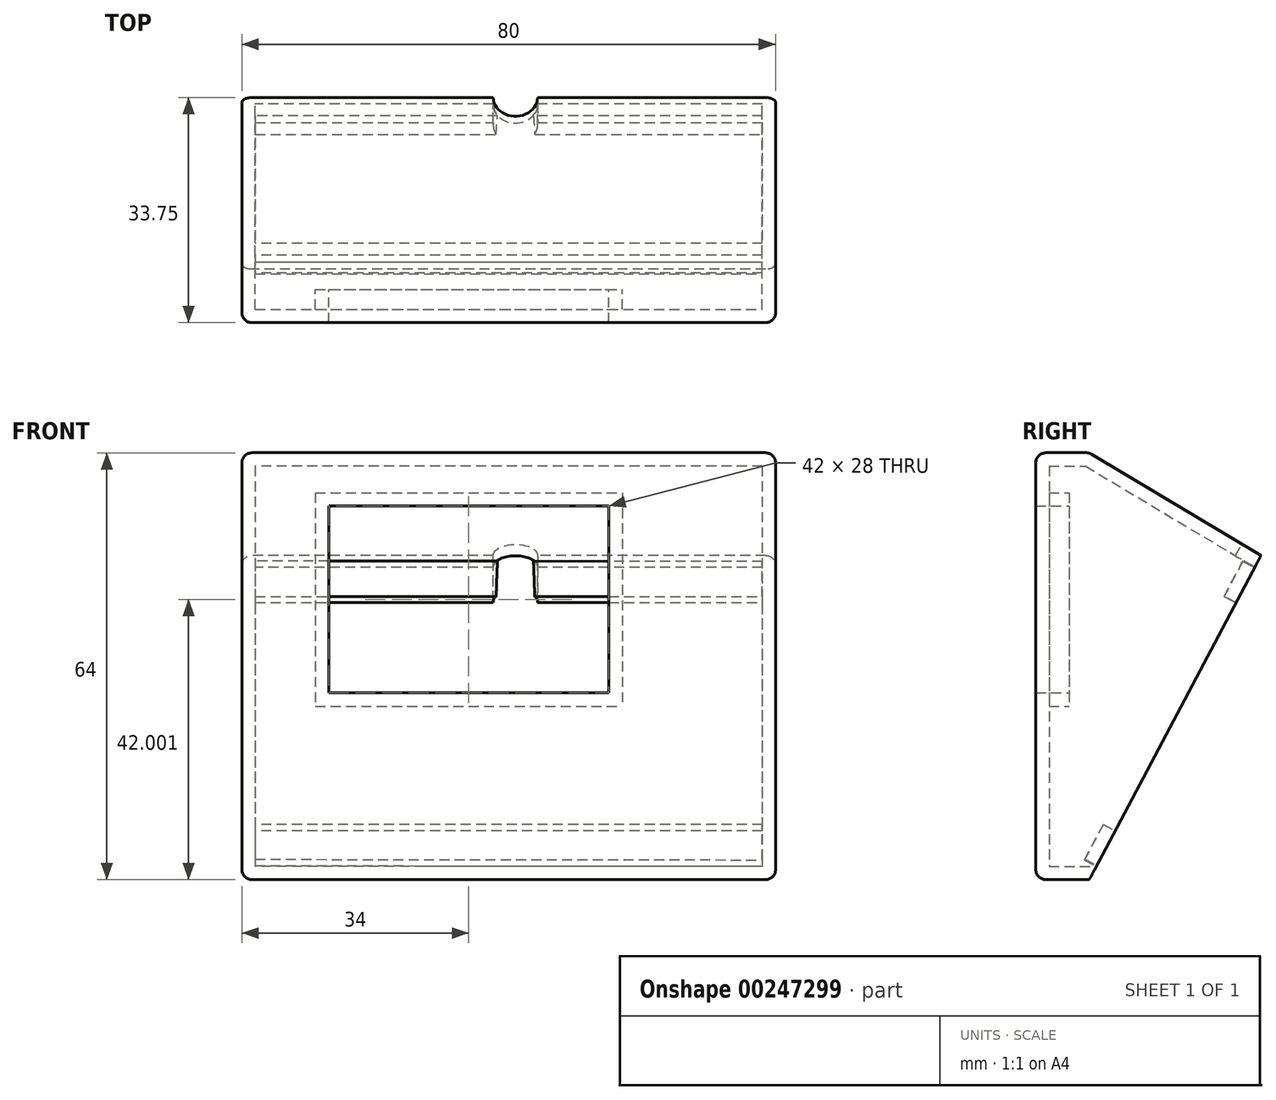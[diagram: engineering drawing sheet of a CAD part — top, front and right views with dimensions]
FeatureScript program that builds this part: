
annotation { "Feature Type Name" : "Feature", "Feature Type Description" : "" }
export const myFeature = defineFeature(function(context is Context, id is Id, definition is map)
    precondition{}
    {
        {
            var Q0;
            Q0=qCreatedBy(makeId("Front.planeOp"),FACE);
            var sketch = newSketch(context, id + "F0", { "sketchPlane" : qUnion([Q0])});
            skLineSegment(sketch, "E0.bottom", {"start": v(-41, 33.96) * mm, "end": v(39, 33.96) * mm});
            skLineSegment(sketch, "E0.top", {"start": v(-41, -30.04) * mm, "end": v(39, -30.04) * mm});
            skLineSegment(sketch, "E0.left", {"start": v(-41, 33.96) * mm, "end": v(-41, -30.04) * mm});
            skLineSegment(sketch, "E0.right", {"start": v(39, 33.96) * mm, "end": v(39, -30.04) * mm});
            skLineSegment(sketch, "E1.bottom", {"start": v(-28, 25.96) * mm, "end": v(14, 25.96) * mm});
            skLineSegment(sketch, "E1.top", {"start": v(-28, -2.04) * mm, "end": v(14, -2.04) * mm});
            skLineSegment(sketch, "E1.left", {"start": v(-28, 25.96) * mm, "end": v(-28, -2.04) * mm});
            skLineSegment(sketch, "E1.right", {"start": v(14, 25.96) * mm, "end": v(14, -2.04) * mm});
            skSolve(sketch);
        }
        {
            var Q0;
            Q0=makeQuery(id+"F0.imprint","IMPRINT",FACE,{"disambiguationData":[TD([[makeQuery(id+"F0.imprint","IMPRINT",EDGE,{"derivedFrom":sQuery(id+"F0.wireOp",EDGE,"E0.bottom")}),-1.0]])]});
            extrude(context, id + "F1", {"entities" : qUnion([Q0]), "depth" : 3 * mm});
        }
        {
            var Q0;
            Q0=makeQuery(id+"F1.opExtrude","SWEPT_FACE",FACE,{"disambiguationData":[OSD([sQuery(id+"F0.wireOp",EDGE,"E0.left")])]});
            cPlane(context, id + "F2", {"entities" : qUnion([Q0]), "cplaneType" : CPlaneType.OFFSET, "offset" : 0 * mm, "width" : 150 * mm, "height" : 150 * mm});
        }
        {
            var Q0;
            Q0=qCreatedBy(id+"F2.planeOp",FACE);
            var sketch = newSketch(context, id + "F3", { "sketchPlane" : qUnion([Q0])});
            skLineSegment(sketch, "E2", {"start": v(0, 33.96) * mm, "end": v(-5, 33.96) * mm});
            skLineSegment(sketch, "E3", {"start": v(-5, 33.96) * mm, "end": v(-30.75, 18.56) * mm});
            skLineSegment(sketch, "E4", {"start": v(-30.75, 18.56) * mm, "end": v(-5, -30.04) * mm});
            skLineSegment(sketch, "E5", {"start": v(-5, -30.04) * mm, "end": v(0, -30.04) * mm});
            skLineSegment(sketch, "E6", {"start": v(0, -30.04) * mm, "end": v(0, 33.96) * mm});
            skSolve(sketch);
        }
        {
            var Q0;
            Q0=makeQuery(id+"F3.imprint","IMPRINT",FACE,{"disambiguationData":[TD([[makeQuery(id+"F3.imprint","IMPRINT",EDGE,{"derivedFrom":sQuery(id+"F3.wireOp",EDGE,"E2")}),1.0]])]});
            extrude(context, id + "F4", {"entities" : qUnion([Q0]), "operationType" : NewBodyOperationType.ADD, "oppositeDirection" : true, "depth" : 80 * mm});
        }
        {
            var Q0;
            Q0=makeQuery(id+"F4.opExtrude","SWEPT_FACE",FACE,{"disambiguationData":[OSD([sQuery(id+"F3.wireOp",EDGE,"E4")])]});
            shell(context, id + "F5", {"entities" : qUnion([Q0]), "thickness" : 2 * mm});
        }
        {
            var Q0;
            Q0=makeQuery(id+"F0.imprint","IMPRINT",FACE,{"disambiguationData":[TD([[makeQuery(id+"F0.imprint","IMPRINT",EDGE,{"derivedFrom":sQuery(id+"F0.wireOp",EDGE,"tYb5kqSu-YFri-1jrc-o4Oq-ESpyQk4ThZfy")}),1.0]])]});
            var Q1;
            Q1=makeQuery(id+"F0.imprint","IMPRINT",FACE,{"disambiguationData":[TD([[makeQuery(id+"F0.imprint","IMPRINT",EDGE,{"derivedFrom":sQuery(id+"F0.wireOp",EDGE,"0d1e089b-857e-4050-88c1-200f67481d80")}),1.0]])]});
            var Q2;
            Q2=makeQuery(id+"F0.imprint","IMPRINT",FACE,{"disambiguationData":[TD([[makeQuery(id+"F0.imprint","IMPRINT",EDGE,{"derivedFrom":sQuery(id+"F0.wireOp",EDGE,"e7074c25-9ab7-490e-b367-edef4363bac3")}),1.0]])]});
            var Q3;
            Q3=makeQuery(id+"F0.imprint","IMPRINT",FACE,{"disambiguationData":[TD([[makeQuery(id+"F0.imprint","IMPRINT",EDGE,{"derivedFrom":sQuery(id+"F0.wireOp",EDGE,"ab4bee96-640a-41a6-9e68-64fc1a0f792d")}),1.0]])]});
            var Q4;
            Q4=makeQuery(id+"F0.imprint","IMPRINT",FACE,{"disambiguationData":[TD([[makeQuery(id+"F0.imprint","IMPRINT",EDGE,{"derivedFrom":sQuery(id+"F0.wireOp",EDGE,"636ad2b5-b186-44ca-803b-94d0a85fc76c")}),1.0]])]});
            var Q5;
            Q5=makeQuery(id+"F0.imprint","IMPRINT",FACE,{"disambiguationData":[TD([[makeQuery(id+"F0.imprint","IMPRINT",EDGE,{"derivedFrom":sQuery(id+"F0.wireOp",EDGE,"E1.bottom")}),-1.0]])]});
            extrude(context, id + "F6", {"entities" : qUnion([Q0, Q1, Q2, Q3, Q4, Q5]), "operationType" : NewBodyOperationType.REMOVE, "oppositeDirection" : true, "depth" : 5 * mm});
        }
        {
            var Q0;
            Q0=makeQuery(id+"F1.opExtrude","CAP_EDGE",EDGE,{"disambiguationData":[OSD([sQuery(id+"F0.wireOp",EDGE,"E0.right")])],"isStart":false});
            var Q1;
            Q1=makeQuery(id+"F4.boolean.opBoolean","MERGE",EDGE,{"derivedFrom":[makeQuery(id+"F1.opExtrude","SWEPT_EDGE",EDGE,{"disambiguationData":[OSD([sQuery(id+"F0.wireOp",EDGE,"E0.top"),sQuery(id+"F0.wireOp",EDGE,"E0.right")])]}),makeQuery(id+"F4.opExtrude","CAP_EDGE",EDGE,{"disambiguationData":[OSD([sQuery(id+"F3.wireOp",EDGE,"E5")])],"isStart":false})]});
            var Q2;
            Q2=makeQuery(id+"F1.opExtrude","CAP_EDGE",EDGE,{"disambiguationData":[OSD([sQuery(id+"F0.wireOp",EDGE,"E0.top")])],"isStart":false});
            var Q3;
            Q3=makeQuery(id+"F4.boolean.opBoolean","MERGE",EDGE,{"derivedFrom":[makeQuery(id+"F1.opExtrude","SWEPT_EDGE",EDGE,{"disambiguationData":[OSD([sQuery(id+"F0.wireOp",EDGE,"E0.bottom"),sQuery(id+"F0.wireOp",EDGE,"E0.right")])]}),makeQuery(id+"F4.opExtrude","CAP_EDGE",EDGE,{"disambiguationData":[OSD([sQuery(id+"F3.wireOp",EDGE,"E2")])],"isStart":false})]});
            var Q4;
            Q4=makeQuery(id+"F4.opExtrude","CAP_EDGE",EDGE,{"disambiguationData":[OSD([sQuery(id+"F3.wireOp",EDGE,"E3")])],"isStart":false});
            var Q5;
            Q5=makeQuery(id+"F1.opExtrude","CAP_EDGE",EDGE,{"disambiguationData":[OSD([sQuery(id+"F0.wireOp",EDGE,"E0.bottom")])],"isStart":false});
            var Q6;
            Q6=makeQuery(id+"F4.opExtrude","SWEPT_EDGE",EDGE,{"disambiguationData":[OSD([sQuery(id+"F3.wireOp",EDGE,"E2"),sQuery(id+"F3.wireOp",EDGE,"E3")])]});
            var Q7;
            Q7=makeQuery(id+"F1.opExtrude","CAP_EDGE",EDGE,{"disambiguationData":[OSD([sQuery(id+"F0.wireOp",EDGE,"E0.left")])],"isStart":false});
            var Q8;
            Q8=makeQuery(id+"F4.boolean.opBoolean","MERGE",EDGE,{"derivedFrom":[makeQuery(id+"F1.opExtrude","SWEPT_EDGE",EDGE,{"disambiguationData":[OSD([sQuery(id+"F0.wireOp",EDGE,"E0.bottom"),sQuery(id+"F0.wireOp",EDGE,"E0.left")])]}),makeQuery(id+"F4.opExtrude","CAP_EDGE",EDGE,{"disambiguationData":[OSD([sQuery(id+"F3.wireOp",EDGE,"E2")])],"isStart":true})]});
            var Q9;
            Q9=makeQuery(id+"F4.opExtrude","CAP_EDGE",EDGE,{"disambiguationData":[OSD([sQuery(id+"F3.wireOp",EDGE,"E3")])],"isStart":true});
            var Q10;
            Q10=makeQuery(id+"F4.boolean.opBoolean","MERGE",EDGE,{"derivedFrom":[makeQuery(id+"F1.opExtrude","SWEPT_EDGE",EDGE,{"disambiguationData":[OSD([sQuery(id+"F0.wireOp",EDGE,"E0.top"),sQuery(id+"F0.wireOp",EDGE,"E0.left")])]}),makeQuery(id+"F4.opExtrude","CAP_EDGE",EDGE,{"disambiguationData":[OSD([sQuery(id+"F3.wireOp",EDGE,"E5")])],"isStart":true})]});
            fillet(context, id + "F7", {"entities" : qUnion([Q0, Q1, Q2, Q3, Q4, Q5, Q6, Q7, Q8, Q9, Q10]), "radius" : 1.5 * mm, "tangentPropagation" : true, "allowEdgeOverflow" : false});
        }
        {
            var Q0;
            Q0=makeQuery(id+"F1.opExtrude","SWEPT_BODY",BODY,{"disambiguationData":[OSD([sQuery(id+"F0.wireOp",EDGE,"E0.bottom"),sQuery(id+"F0.wireOp",EDGE,"E0.top"),sQuery(id+"F0.wireOp",EDGE,"E0.left"),sQuery(id+"F0.wireOp",EDGE,"E0.right"),sQuery(id+"F0.wireOp",EDGE,"tYb5kqSu-YFri-1jrc-o4Oq-ESpyQk4ThZfy"),sQuery(id+"F0.wireOp",EDGE,"0d1e089b-857e-4050-88c1-200f67481d80"),sQuery(id+"F0.wireOp",EDGE,"e7074c25-9ab7-490e-b367-edef4363bac3"),sQuery(id+"F0.wireOp",EDGE,"ab4bee96-640a-41a6-9e68-64fc1a0f792d"),sQuery(id+"F0.wireOp",EDGE,"636ad2b5-b186-44ca-803b-94d0a85fc76c"),sQuery(id+"F0.wireOp",EDGE,"E1.bottom"),sQuery(id+"F0.wireOp",EDGE,"E1.top"),sQuery(id+"F0.wireOp",EDGE,"E1.left"),sQuery(id+"F0.wireOp",EDGE,"E1.right")])]});
            transform(context, id + "F8", {"entities" : qUnion([Q0]), "transformType" : TransformType.TRANSLATION_3D, "dx" : 0 * mm, "dy" : 0 * mm, "dz" : 0 * mm, "makeCopy" : true});
        }
        {
            var Q0;
            Q0=makeQuery(id+"F8.opPattern","COPY",BODY,{"derivedFrom":makeQuery(id+"F1.opExtrude","SWEPT_BODY",BODY,{"disambiguationData":[OSD([sQuery(id+"F0.wireOp",EDGE,"E0.bottom"),sQuery(id+"F0.wireOp",EDGE,"E0.top"),sQuery(id+"F0.wireOp",EDGE,"E0.left"),sQuery(id+"F0.wireOp",EDGE,"E0.right"),sQuery(id+"F0.wireOp",EDGE,"tYb5kqSu-YFri-1jrc-o4Oq-ESpyQk4ThZfy"),sQuery(id+"F0.wireOp",EDGE,"0d1e089b-857e-4050-88c1-200f67481d80"),sQuery(id+"F0.wireOp",EDGE,"e7074c25-9ab7-490e-b367-edef4363bac3"),sQuery(id+"F0.wireOp",EDGE,"ab4bee96-640a-41a6-9e68-64fc1a0f792d"),sQuery(id+"F0.wireOp",EDGE,"636ad2b5-b186-44ca-803b-94d0a85fc76c"),sQuery(id+"F0.wireOp",EDGE,"E1.bottom"),sQuery(id+"F0.wireOp",EDGE,"E1.top"),sQuery(id+"F0.wireOp",EDGE,"E1.left"),sQuery(id+"F0.wireOp",EDGE,"E1.right")])]}),"instanceName":"1"});
            deleteBodies(context, id + "F9", {"entities" : qUnion([Q0])});
        }
        {
            var Q0;
            Q0=makeQuery(id+"F4.opExtrude","SWEPT_FACE",FACE,{"disambiguationData":[OSD([sQuery(id+"F3.wireOp",EDGE,"E4")])]});
            cPlane(context, id + "F10", {"entities" : qUnion([Q0]), "cplaneType" : CPlaneType.OFFSET, "offset" : 0 * mm, "width" : 150 * mm, "height" : 150 * mm});
        }
        {
            var Q0;
            Q0=qCreatedBy(id+"F10.planeOp",FACE);
            var sketch = newSketch(context, id + "F11", { "sketchPlane" : qUnion([Q0])});
            skLineSegment(sketch, "E7.right", {"start": v(39, 28.8) * mm, "end": v(39, 22.8) * mm});
            skLineSegment(sketch, "E8", {"start": v(39, 22.8) * mm, "end": v(-37, 22.8) * mm});
            skLineSegment(sketch, "E9", {"start": v(-37, 22.8) * mm, "end": v(-37, 28.75) * mm});
            skLineSegment(sketch, "E10", {"start": v(-37, 28.75) * mm, "end": v(39, 28.8) * mm});
            skLineSegment(sketch, "E11", {"start": v(-37, -21.9) * mm, "end": v(-37, -15.91) * mm});
            skLineSegment(sketch, "E12", {"start": v(-37, -15.91) * mm, "end": v(39, -15.91) * mm});
            skLineSegment(sketch, "E13", {"start": v(39, -15.91) * mm, "end": v(39, -21.82) * mm});
            skLineSegment(sketch, "E14", {"start": v(39, -21.82) * mm, "end": v(-37, -21.9) * mm});
            skSolve(sketch);
        }
        {
            var Q0;
            Q0=makeQuery(id+"F11.imprint","IMPRINT",FACE,{"disambiguationData":[TD([[makeQuery(id+"F11.imprint","IMPRINT",EDGE,{"derivedFrom":sQuery(id+"F11.wireOp",EDGE,"E11")}),-1.0]])]});
            extrude(context, id + "F12", {"entities" : qUnion([Q0]), "operationType" : NewBodyOperationType.ADD, "oppositeDirection" : true, "depth" : 2 * mm});
        }
        {
            var Q0;
            Q0=makeQuery(id+"F11.imprint","IMPRINT",FACE,{"disambiguationData":[TD([[makeQuery(id+"F11.imprint","IMPRINT",EDGE,{"derivedFrom":sQuery(id+"F11.wireOp",EDGE,"E7.right")}),-1.0]])]});
            extrude(context, id + "F13", {"entities" : qUnion([Q0]), "operationType" : NewBodyOperationType.ADD, "oppositeDirection" : true, "depth" : 2 * mm});
        }
        {
            var Q0;
            Q0=makeQuery(id+"F4.opExtrude","SWEPT_FACE",FACE,{"disambiguationData":[OSD([sQuery(id+"F3.wireOp",EDGE,"E3")])]});
            cPlane(context, id + "F14", {"entities" : qUnion([Q0]), "cplaneType" : CPlaneType.OFFSET, "offset" : 0 * mm, "width" : 150 * mm, "height" : 150 * mm});
        }
        {
            var Q0;
            Q0=qCreatedBy(id+"F14.planeOp",FACE);
            var sketch = newSketch(context, id + "F15", { "sketchPlane" : qUnion([Q0])});
            skCircle(sketch, "E15", {"center": v(0, 16.92) * mm, "radius": 3.33 * mm});
            skSolve(sketch);
        }
        {
            var Q0;
            Q0=makeQuery(id+"F15.imprint","IMPRINT",FACE,{"disambiguationData":[TD([[makeQuery(id+"F15.imprint","IMPRINT",EDGE,{"derivedFrom":sQuery(id+"F15.wireOp",EDGE,"E15")}),1.0]])]});
            extrude(context, id + "F16", {"entities" : qUnion([Q0]), "operationType" : NewBodyOperationType.REMOVE, "oppositeDirection" : true, "depth" : 25 * mm});
        }
    });
